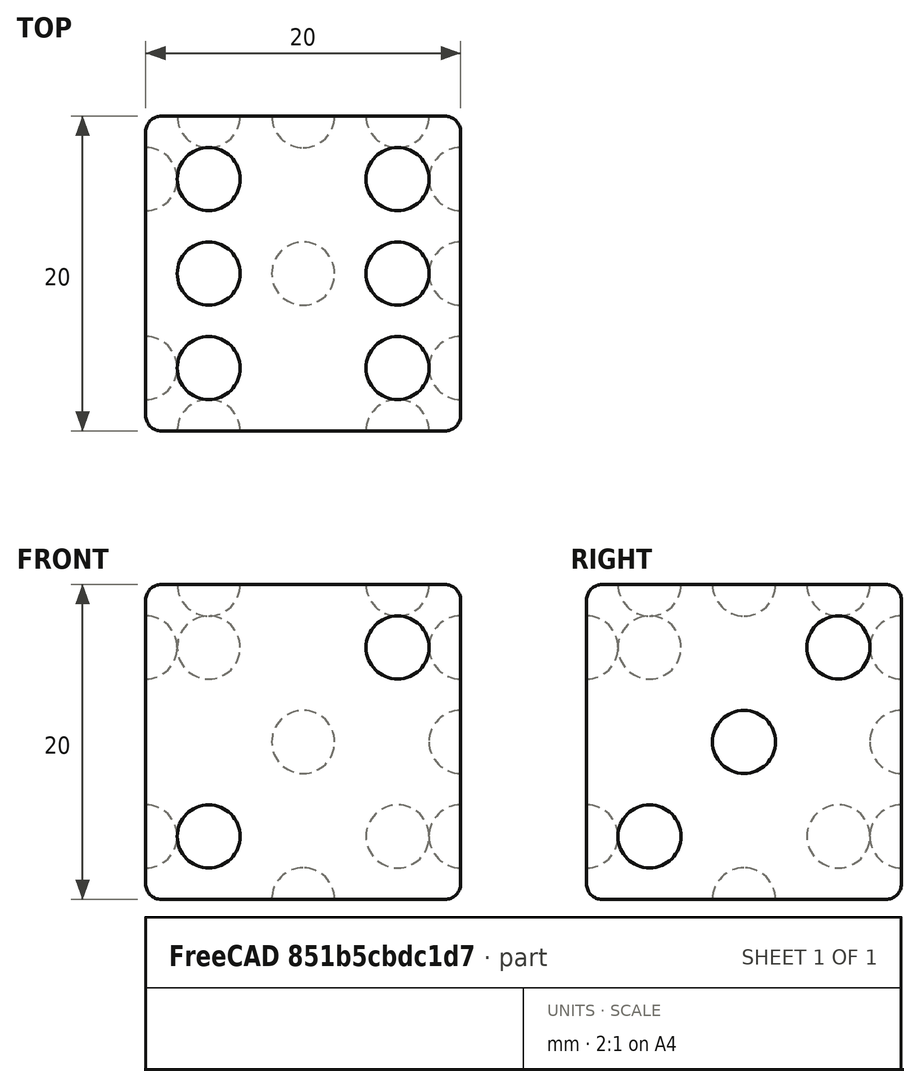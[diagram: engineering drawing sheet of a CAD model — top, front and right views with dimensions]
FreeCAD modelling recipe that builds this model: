
FCSTD DOCUMENT  (FreeCAD 0.18.4R)
Label: tutorial_freecad_ex13_c
License: All rights reserved
LicenseURL: http://en.wikipedia.org/wiki/All_rights_reserved
objects: Part::Sphere×7, Part::FeaturePython×5, Part::MultiFuse×2, Part::Box×1, Part::Fillet×1, Part::Cut×1
note: 17 computed .brp shape members not serialized (recipe doc carries the construction recipe); baked Part::Feature solids carry a one-line shape summary decoded from their .brp

FEATURE [Part::Box] Box  label="Cubo"
  AttacherType = Attacher::AttachEngine3D
  Height = 20
  Length = 20
  Width = 20
FEATURE [Part::Fillet] Fillet  label="cubo"
  Base = -> Box
  Edges = 12 edges r=1: [Edge1,Edge2,Edge3,Edge4,Edge5,Edge6,Edge7,Edge8,Edge9,Edge10,Edge11,Edge12]
FEATURE [Part::Sphere] Sphere  label="Esfera"
  Angle1 = -90
  Angle2 = 90
  Angle3 = 360
  AttacherType = Attacher::AttachEngine3D
  Radius = 2
FEATURE [Part::Sphere] Sphere001  label="Esfera001"
  Angle1 = -90
  Angle2 = 90
  Angle3 = 360
  AttacherType = Attacher::AttachEngine3D
  Radius = 2
FEATURE [Part::FeaturePython] Array001  label="cuatro"  # Draft array (typed FeaturePython)
  Angle = 360
  ArrayType = 0
  Axis = (0,0,1)
  Base = -> Sphere001
  Center = (0,0,0)
  Fuse = false
  IntervalAxis = (0,0,0)
  IntervalX = (12,0,0)
  IntervalY = (0,12,0)
  IntervalZ = (0,0,1)
  NumberPolar = 1
  NumberX = 2
  NumberY = 2
  NumberZ = 1
  Placement = pos=(0,4,16) rot=(0,1,0;1.5708rad)
FEATURE [Part::Sphere] Sphere002  label="Esfera002"
  Angle1 = -90
  Angle2 = 90
  Angle3 = 360
  AttacherType = Attacher::AttachEngine3D
  Radius = 2
FEATURE [Part::FeaturePython] Array002  label="tres"  # Draft array (typed FeaturePython)
  Angle = 360
  ArrayType = 0
  Axis = (0,0,1)
  Base = -> Sphere002
  Center = (0,0,0)
  Fuse = false
  IntervalAxis = (0,0,0)
  IntervalX = (6,6,0)
  IntervalY = (0,12,0)
  IntervalZ = (0,0,1)
  NumberPolar = 1
  NumberX = 3
  NumberY = 1
  NumberZ = 1
  Placement = pos=(20,4,4) rot=(0,1,0;4.71239rad)
FEATURE [Part::Sphere] Sphere003  label="Esfera003"
  Angle1 = -90
  Angle2 = 90
  Angle3 = 360
  AttacherType = Attacher::AttachEngine3D
  Radius = 2
FEATURE [Part::FeaturePython] Array003  label="dos"  # Draft array (typed FeaturePython)
  Angle = 360
  ArrayType = 0
  Axis = (0,0,1)
  Base = -> Sphere003
  Center = (0,0,0)
  Fuse = false
  IntervalAxis = (0,0,0)
  IntervalX = (12,12,0)
  IntervalY = (0,12,0)
  IntervalZ = (0,0,1)
  NumberPolar = 1
  NumberX = 2
  NumberY = 1
  NumberZ = 1
  Placement = pos=(4,0,4) rot=(1,0,0;1.5708rad)
FEATURE [Part::Sphere] Sphere004  label="uno"
  Angle1 = -90
  Angle2 = 90
  Angle3 = 360
  AttacherType = Attacher::AttachEngine3D
  Placement = pos=(10,10,0) rot=(0,0,1;0rad)
  Radius = 2
FEATURE [Part::FeaturePython] Array  label="seis"  # Draft array (typed FeaturePython)
  Angle = 360
  ArrayType = 0
  Axis = (0,0,1)
  Base = -> Sphere
  Center = (0,0,0)
  Fuse = false
  IntervalAxis = (0,0,0)
  IntervalX = (6,0,0)
  IntervalY = (0,12,0)
  IntervalZ = (0,0,1)
  NumberPolar = 1
  NumberX = 3
  NumberY = 2
  NumberZ = 1
  Placement = pos=(16,4,20) rot=(0,0,1;1.5708rad)
FEATURE [Part::Sphere] Sphere005  label="uno001"
  Angle1 = -90
  Angle2 = 90
  Angle3 = 360
  AttacherType = Attacher::AttachEngine3D
  Placement = pos=(10,10,20) rot=(0,0,1;0rad)
  Radius = 2
FEATURE [Part::Sphere] Sphere006  label="Esfera004"
  Angle1 = -90
  Angle2 = 90
  Angle3 = 360
  AttacherType = Attacher::AttachEngine3D
  Radius = 2
FEATURE [Part::FeaturePython] Array004  label="cuatro001"  # Draft array (typed FeaturePython)
  Angle = 360
  ArrayType = 0
  Axis = (0,0,1)
  Base = -> Sphere006
  Center = (0,0,0)
  Fuse = false
  IntervalAxis = (0,0,0)
  IntervalX = (12,0,0)
  IntervalY = (0,12,0)
  IntervalZ = (0,0,1)
  NumberPolar = 1
  NumberX = 2
  NumberY = 2
  NumberZ = 1
  Placement = pos=(4,4,20) rot=(0,1,0;0rad)
FEATURE [Part::MultiFuse] Fusion  label="cinco"
  Placement = pos=(0,40,0) rot=(1,0,0;1.5708rad)
  Refine = true
  Shapes = -> [Sphere005,Array004]
FEATURE [Part::MultiFuse] Fusion001  label="numeros"
  Refine = true
  Shapes = -> [Array003,Fusion,Sphere004,Array002,Array001,Array]
FEATURE [Part::Cut] Cut  label="dado"
  Base = -> Fillet
  Refine = true
  Tool = -> Fusion001
